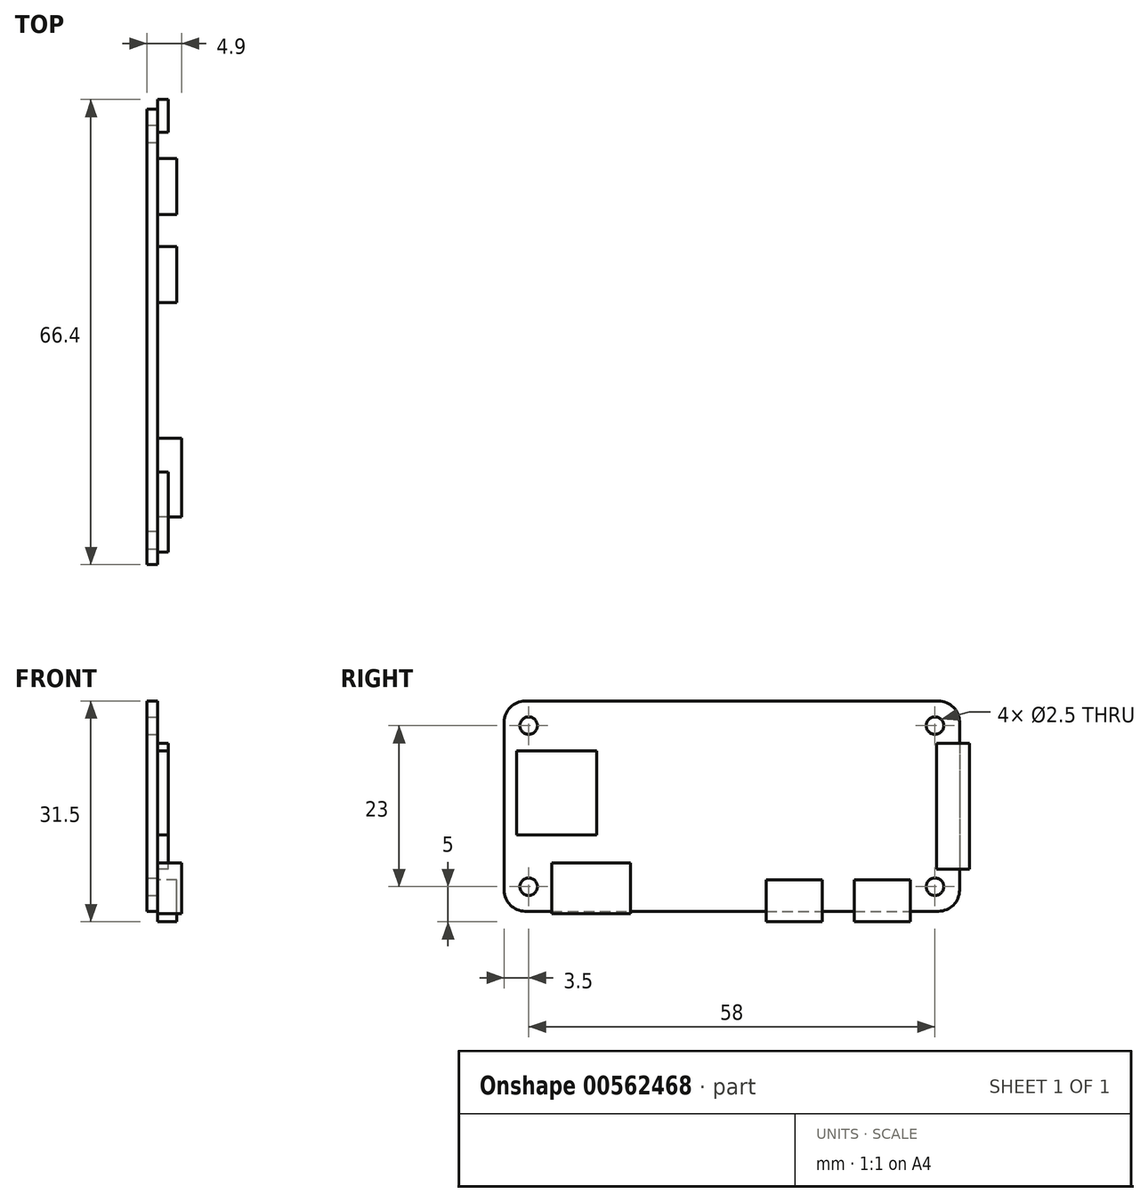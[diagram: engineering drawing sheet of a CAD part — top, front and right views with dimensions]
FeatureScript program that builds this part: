
annotation { "Feature Type Name" : "Feature", "Feature Type Description" : "" }
export const myFeature = defineFeature(function(context is Context, id is Id, definition is map)
    precondition{}
    {
        {
            var Q0;
            Q0=qCreatedBy(makeId("Right.planeOp"),FACE);
            var sketch = newSketch(context, id + "F0", { "sketchPlane" : qUnion([Q0])});
            skLineSegment(sketch, "E0.bottom", {"start": v(-29.5, 15) * mm, "end": v(29.5, 15) * mm});
            skLineSegment(sketch, "E0.top", {"start": v(-29.5, -15) * mm, "end": v(29.5, -15) * mm});
            skLineSegment(sketch, "E0.left", {"start": v(-32.5, 12) * mm, "end": v(-32.5, -12) * mm});
            skLineSegment(sketch, "E0.right", {"start": v(32.5, 12) * mm, "end": v(32.5, -12) * mm});
            skPoint(sketch, "E0.middle", {"position": v(0, 0) * mm});
            skPoint(sketch, "E1.visualSharp", {"position": v(-32.5, 15) * mm});
            skArc(sketch, "E1.filletArc", {"start": v(-29.5, 15) * mm, "mid": v(-31.62, 14.12) * mm, "end": v(-32.5, 12) * mm});
            skPoint(sketch, "E2.visualSharp", {"position": v(-32.5, -15) * mm});
            skArc(sketch, "E2.filletArc", {"start": v(-32.5, -12) * mm, "mid": v(-31.62, -14.12) * mm, "end": v(-29.5, -15) * mm});
            skPoint(sketch, "E3.visualSharp", {"position": v(32.5, -15) * mm});
            skArc(sketch, "E3.filletArc", {"start": v(29.5, -15) * mm, "mid": v(31.62, -14.12) * mm, "end": v(32.5, -12) * mm});
            skPoint(sketch, "E4.visualSharp", {"position": v(32.5, 15) * mm});
            skArc(sketch, "E4.filletArc", {"start": v(32.5, 12) * mm, "mid": v(31.62, 14.12) * mm, "end": v(29.5, 15) * mm});
            skSolve(sketch);
        }
        {
            var Q0;
            Q0=makeQuery(id+"F0.imprint","IMPRINT",FACE,{"disambiguationData":[TD([[makeQuery(id+"F0.imprint","IMPRINT",EDGE,{"derivedFrom":sQuery(id+"F0.wireOp",EDGE,"E0.bottom")}),-1.0]])]});
            extrude(context, id + "F1", {"entities" : qUnion([Q0]), "depth" : 1.5 * mm, "offsetDistance" : 25 * mm, "symmetric" : true});
        }
        {
            var Q0;
            Q0=makeQuery(id+"F1.opExtrude","CAP_FACE",FACE,{"disambiguationData":[OSD([sQuery(id+"F0.wireOp",EDGE,"E0.bottom"),sQuery(id+"F0.wireOp",EDGE,"E0.top"),sQuery(id+"F0.wireOp",EDGE,"E0.left"),sQuery(id+"F0.wireOp",EDGE,"E0.right"),sQuery(id+"F0.wireOp",EDGE,"E1.filletArc"),sQuery(id+"F0.wireOp",EDGE,"E2.filletArc"),sQuery(id+"F0.wireOp",EDGE,"E3.filletArc"),sQuery(id+"F0.wireOp",EDGE,"E4.filletArc")])],"isStart":false});
            var sketch = newSketch(context, id + "F2", { "sketchPlane" : qUnion([Q0])});
            skCircle(sketch, "E5", {"center": v(-29, 11.5) * mm, "radius": 1.25 * mm});
            skCircle(sketch, "E6", {"center": v(29, 11.5) * mm, "radius": 1.25 * mm});
            skCircle(sketch, "E7", {"center": v(29, -11.5) * mm, "radius": 1.25 * mm});
            skCircle(sketch, "E8", {"center": v(-29, -11.5) * mm, "radius": 1.25 * mm});
            skSolve(sketch);
        }
        {
            var Q0;
            Q0 = qSketchRegion(id + "F2", true);
            var Q1;
            Q1=makeQuery(id+"F1.opExtrude","CAP_FACE",FACE,{"disambiguationData":[OSD([sQuery(id+"F0.wireOp",EDGE,"E0.bottom"),sQuery(id+"F0.wireOp",EDGE,"E0.top"),sQuery(id+"F0.wireOp",EDGE,"E0.left"),sQuery(id+"F0.wireOp",EDGE,"E0.right"),sQuery(id+"F0.wireOp",EDGE,"E1.filletArc"),sQuery(id+"F0.wireOp",EDGE,"E2.filletArc"),sQuery(id+"F0.wireOp",EDGE,"E3.filletArc"),sQuery(id+"F0.wireOp",EDGE,"E4.filletArc")])],"isStart":true});
            extrude(context, id + "F3", {"entities" : qUnion([Q0]), "operationType" : NewBodyOperationType.REMOVE, "endBound" : BoundingType.UP_TO_SURFACE, "oppositeDirection" : true, "depth" : 25 * mm, "endBoundEntityFace" : qUnion([Q1]), "offsetDistance" : 25 * mm});
        }
        {
            var Q0;
            Q0=makeQuery(id+"F1.opExtrude","CAP_FACE",FACE,{"disambiguationData":[OSD([sQuery(id+"F0.wireOp",EDGE,"E0.bottom"),sQuery(id+"F0.wireOp",EDGE,"E0.top"),sQuery(id+"F0.wireOp",EDGE,"E0.left"),sQuery(id+"F0.wireOp",EDGE,"E0.right"),sQuery(id+"F0.wireOp",EDGE,"E1.filletArc"),sQuery(id+"F0.wireOp",EDGE,"E2.filletArc"),sQuery(id+"F0.wireOp",EDGE,"E3.filletArc"),sQuery(id+"F0.wireOp",EDGE,"E4.filletArc")])],"isStart":false});
            var sketch = newSketch(context, id + "F4", { "sketchPlane" : qUnion([Q0])});
            skLineSegment(sketch, "E9.bottom", {"start": v(-14.47, -15.35) * mm, "end": v(-25.72, -15.35) * mm});
            skLineSegment(sketch, "E9.top", {"start": v(-14.48, -8.1) * mm, "end": v(-25.73, -8.1) * mm});
            skLineSegment(sketch, "E9.left", {"start": v(-14.47, -15.35) * mm, "end": v(-14.48, -8.1) * mm});
            skLineSegment(sketch, "E9.right", {"start": v(-25.73, -15.35) * mm, "end": v(-25.73, -8.1) * mm});
            skPoint(sketch, "E9.middle", {"position": v(-20.1, -11.72) * mm});
            skLineSegment(sketch, "E10.bottom", {"start": v(12.9, -16.5) * mm, "end": v(4.9, -16.5) * mm});
            skLineSegment(sketch, "E10.top", {"start": v(12.9, -10.5) * mm, "end": v(4.9, -10.5) * mm});
            skLineSegment(sketch, "E10.left", {"start": v(12.9, -16.5) * mm, "end": v(12.9, -10.5) * mm});
            skLineSegment(sketch, "E10.right", {"start": v(4.9, -16.5) * mm, "end": v(4.9, -10.5) * mm});
            skPoint(sketch, "E10.middle", {"position": v(8.9, -13.5) * mm});
            skLineSegment(sketch, "E11.bottom", {"start": v(17.5, -10.5) * mm, "end": v(25.5, -10.5) * mm});
            skLineSegment(sketch, "E11.top", {"start": v(17.5, -16.5) * mm, "end": v(25.5, -16.5) * mm});
            skLineSegment(sketch, "E11.left", {"start": v(17.5, -10.5) * mm, "end": v(17.5, -16.5) * mm});
            skLineSegment(sketch, "E11.right", {"start": v(25.5, -10.5) * mm, "end": v(25.5, -16.5) * mm});
            skPoint(sketch, "E11.middle", {"position": v(21.5, -13.5) * mm});
            skLineSegment(sketch, "E12.bottom", {"start": v(33.9, -9) * mm, "end": v(29.2, -9) * mm});
            skLineSegment(sketch, "E12.top", {"start": v(33.9, 9) * mm, "end": v(29.2, 9) * mm});
            skLineSegment(sketch, "E12.left", {"start": v(33.9, -9) * mm, "end": v(33.9, 9) * mm});
            skLineSegment(sketch, "E12.right", {"start": v(29.2, -9) * mm, "end": v(29.2, 9) * mm});
            skPoint(sketch, "E12.middle", {"position": v(31.55, 0) * mm});
            skLineSegment(sketch, "E13.bottom", {"start": v(-30.7, 7.9) * mm, "end": v(-19.3, 7.9) * mm});
            skLineSegment(sketch, "E13.top", {"start": v(-30.7, -4.1) * mm, "end": v(-19.3, -4.1) * mm});
            skLineSegment(sketch, "E13.left", {"start": v(-30.7, 7.9) * mm, "end": v(-30.7, -4.1) * mm});
            skLineSegment(sketch, "E13.right", {"start": v(-19.3, 7.9) * mm, "end": v(-19.3, -4.1) * mm});
            skPoint(sketch, "E13.middle", {"position": v(-25, 1.9) * mm});
            skSolve(sketch);
        }
        {
            var Q0;
            {var subQ0=sQuery(id+"F4.wireOp",EDGE,"E9.bottom");Q0=makeQuery(id+"F4.imprint","IMPRINT",FACE,{"disambiguationData":[TD([[makeQuery(id+"F4.imprint","IMPRINT",EDGE,{"derivedFrom":subQ0}),-1.0]])]});}
            var Q1;
            {var subQ0=sQuery(id+"F4.wireOp",EDGE,"E9.top");Q1=makeQuery(id+"F4.imprint","IMPRINT",FACE,{"disambiguationData":[TD([[makeQuery(id+"F4.imprint","IMPRINT",EDGE,{"derivedFrom":subQ0}),1.0]])]});}
            extrude(context, id + "F5", {"entities" : qUnion([Q0, Q1]), "operationType" : NewBodyOperationType.ADD, "depth" : 3.4 * mm, "offsetDistance" : 25 * mm});
        }
        {
            var Q0;
            {var subQ0=sQuery(id+"F4.wireOp",EDGE,"E10.top");Q0=makeQuery(id+"F4.imprint","IMPRINT",FACE,{"disambiguationData":[TD([[makeQuery(id+"F4.imprint","IMPRINT",EDGE,{"derivedFrom":subQ0}),1.0]])]});}
            var Q1;
            {var subQ0=sQuery(id+"F4.wireOp",EDGE,"E10.bottom");Q1=makeQuery(id+"F4.imprint","IMPRINT",FACE,{"disambiguationData":[TD([[makeQuery(id+"F4.imprint","IMPRINT",EDGE,{"derivedFrom":subQ0}),-1.0]])]});}
            var Q2;
            {var subQ0=sQuery(id+"F4.wireOp",EDGE,"E11.bottom");Q2=makeQuery(id+"F4.imprint","IMPRINT",FACE,{"disambiguationData":[TD([[makeQuery(id+"F4.imprint","IMPRINT",EDGE,{"derivedFrom":subQ0}),-1.0]])]});}
            var Q3;
            {var subQ0=sQuery(id+"F4.wireOp",EDGE,"E11.top");Q3=makeQuery(id+"F4.imprint","IMPRINT",FACE,{"disambiguationData":[TD([[makeQuery(id+"F4.imprint","IMPRINT",EDGE,{"derivedFrom":subQ0}),1.0]])]});}
            extrude(context, id + "F6", {"entities" : qUnion([Q0, Q1, Q2, Q3]), "operationType" : NewBodyOperationType.ADD, "depth" : 2.75 * mm, "offsetDistance" : 25 * mm});
        }
        {
            var Q0;
            {var subQ0=sQuery(id+"F4.wireOp",EDGE,"E12.left");Q0=makeQuery(id+"F4.imprint","IMPRINT",FACE,{"disambiguationData":[TD([[makeQuery(id+"F4.imprint","IMPRINT",EDGE,{"derivedFrom":subQ0}),1.0]])]});}
            var Q1;
            {var subQ0=sQuery(id+"F4.wireOp",EDGE,"E12.right");Q1=makeQuery(id+"F4.imprint","IMPRINT",FACE,{"disambiguationData":[TD([[makeQuery(id+"F4.imprint","IMPRINT",EDGE,{"derivedFrom":subQ0}),-1.0]])]});}
            extrude(context, id + "F7", {"entities" : qUnion([Q0, Q1]), "operationType" : NewBodyOperationType.ADD, "depth" : 1.5 * mm, "offsetDistance" : 25 * mm});
        }
        {
            var Q0;
            Q0=makeQuery(id+"F4.imprint","IMPRINT",FACE,{"disambiguationData":[TD([[makeQuery(id+"F4.imprint","IMPRINT",EDGE,{"derivedFrom":sQuery(id+"F4.wireOp",EDGE,"E13.bottom")}),-1.0]])]});
            extrude(context, id + "F8", {"entities" : qUnion([Q0]), "operationType" : NewBodyOperationType.ADD, "depth" : 1.5 * mm, "offsetDistance" : 25 * mm});
        }
    });
